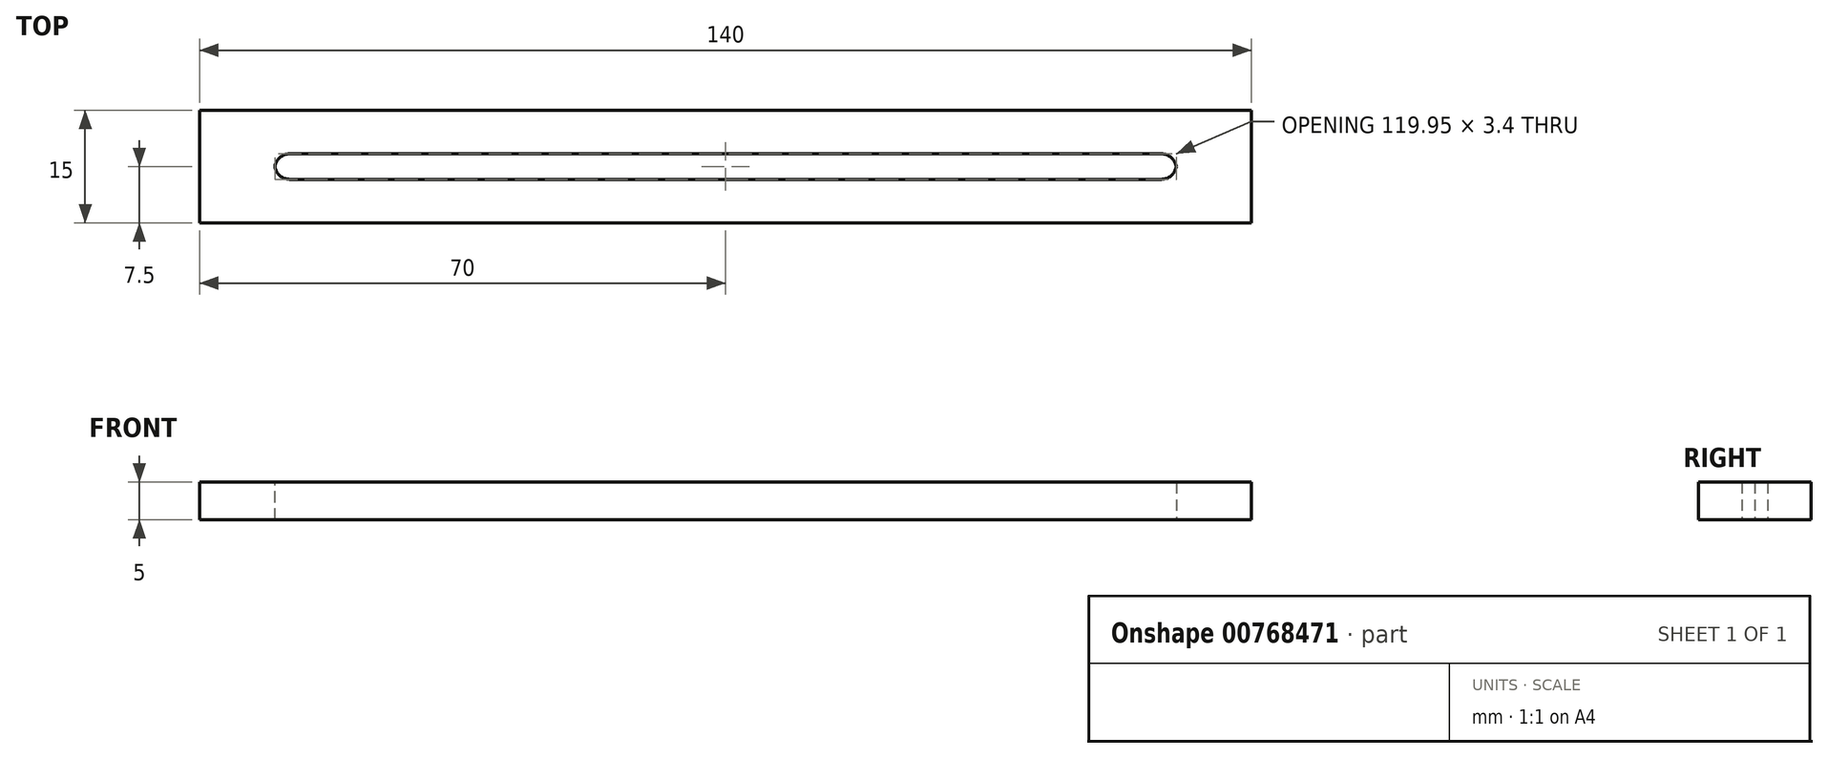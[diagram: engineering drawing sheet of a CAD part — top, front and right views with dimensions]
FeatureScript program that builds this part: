
annotation { "Feature Type Name" : "Feature", "Feature Type Description" : "" }
export const myFeature = defineFeature(function(context is Context, id is Id, definition is map)
    precondition{}
    {
        {
            var Q0;
            Q0=qCreatedBy(makeId("Top.planeOp"),FACE);
            var sketch = newSketch(context, id + "F0", { "sketchPlane" : qUnion([Q0])});
            skLineSegment(sketch, "E0.bottom", {"start": v(70, 7.5) * mm, "end": v(-70, 7.5) * mm});
            skLineSegment(sketch, "E0.top", {"start": v(70, -7.5) * mm, "end": v(-70, -7.5) * mm});
            skLineSegment(sketch, "E0.left", {"start": v(70, 7.5) * mm, "end": v(70, -7.5) * mm});
            skLineSegment(sketch, "E0.right", {"start": v(-70, 7.5) * mm, "end": v(-70, -7.5) * mm});
            skPoint(sketch, "E0.middle", {"position": v(0, 0) * mm});
            skLineSegment(sketch, "E1.bottom", {"start": v(60, 1.7) * mm, "end": v(-60, 1.7) * mm});
            skLineSegment(sketch, "E1.top", {"start": v(60, -1.7) * mm, "end": v(-60, -1.7) * mm});
            skLineSegment(sketch, "E1.left", {"start": v(60, 1.7) * mm, "end": v(60, -1.7) * mm});
            skLineSegment(sketch, "E1.right", {"start": v(-60, 1.7) * mm, "end": v(-60, -1.7) * mm});
            skSolve(sketch);
        }
        {
            var Q0;
            Q0=makeQuery(id+"F0.imprint","IMPRINT",FACE,{"disambiguationData":[TD([[makeQuery(id+"F0.imprint","IMPRINT",EDGE,{"derivedFrom":sQuery(id+"F0.wireOp",EDGE,"E0.bottom")}),1.0]])]});
            extrude(context, id + "F1", {"entities" : qUnion([Q0]), "depth" : 5 * mm, "offsetDistance" : 25 * mm});
        }
        {
            var Q0;
            Q0=makeQuery(id+"F1.opExtrude","SWEPT_EDGE",EDGE,{"disambiguationData":[OSD([sQuery(id+"F0.wireOp",EDGE,"E1.bottom"),sQuery(id+"F0.wireOp",EDGE,"E1.right")])]});
            var Q1;
            Q1=makeQuery(id+"F1.opExtrude","SWEPT_EDGE",EDGE,{"disambiguationData":[OSD([sQuery(id+"F0.wireOp",EDGE,"E1.top"),sQuery(id+"F0.wireOp",EDGE,"E1.right")])]});
            var Q2;
            Q2=makeQuery(id+"F1.opExtrude","SWEPT_EDGE",EDGE,{"disambiguationData":[OSD([sQuery(id+"F0.wireOp",EDGE,"E1.bottom"),sQuery(id+"F0.wireOp",EDGE,"E1.left")])]});
            var Q3;
            Q3=makeQuery(id+"F1.opExtrude","SWEPT_EDGE",EDGE,{"disambiguationData":[OSD([sQuery(id+"F0.wireOp",EDGE,"E1.top"),sQuery(id+"F0.wireOp",EDGE,"E1.left")])]});
            fillet(context, id + "F2", {"entities" : qUnion([Q0, Q1, Q2, Q3]), "tangentPropagation" : true, "radius" : 2 * mm, "defaultsChanged" : true, "vertexSettings" : [], "allowEdgeOverflow" : false});
        }
    });
